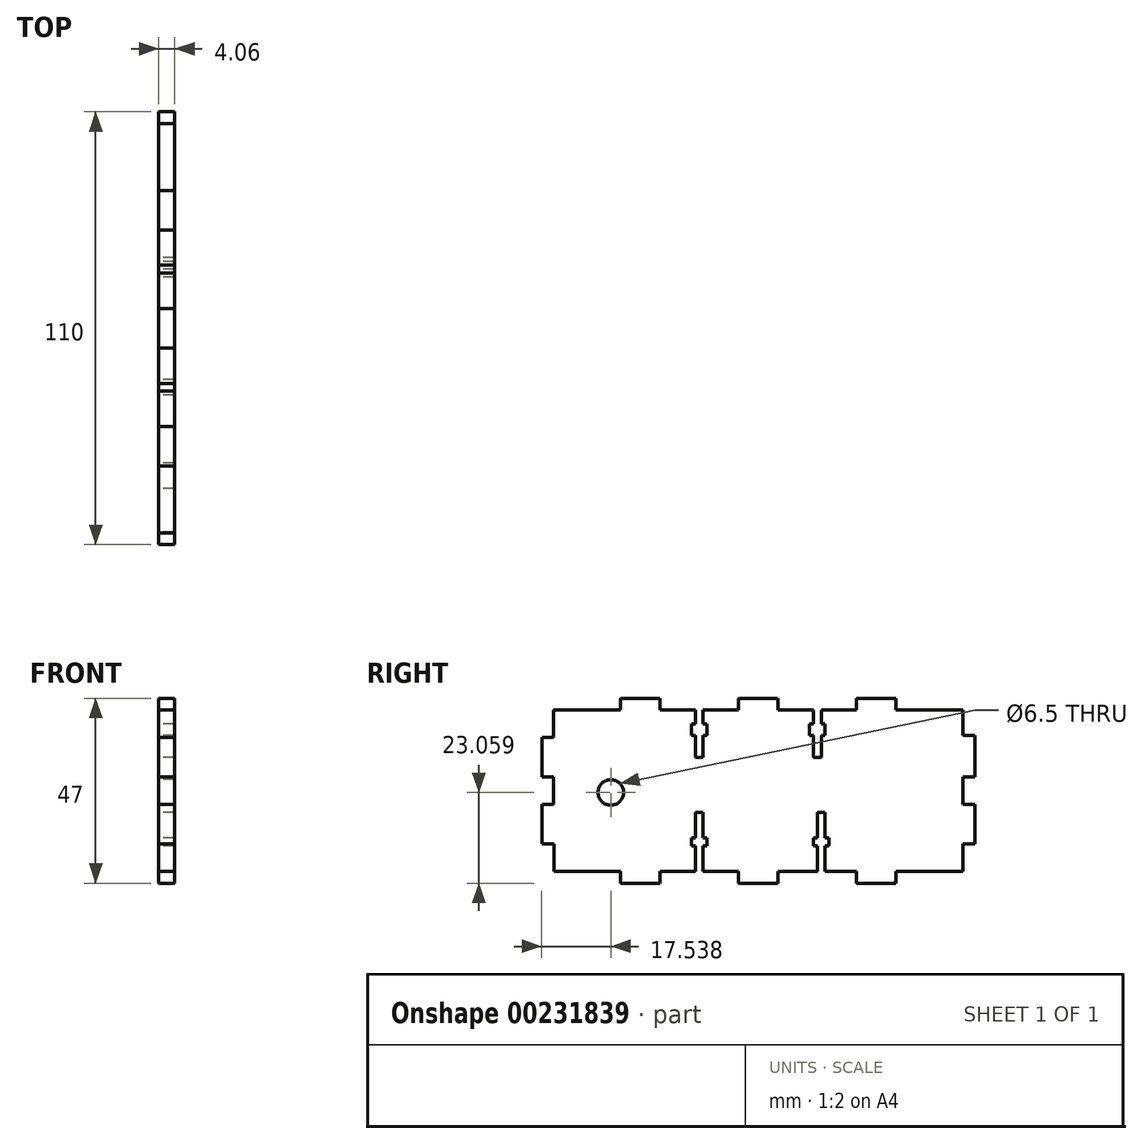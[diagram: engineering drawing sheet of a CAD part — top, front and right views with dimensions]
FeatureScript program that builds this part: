
annotation { "Feature Type Name" : "Feature", "Feature Type Description" : "" }
export const myFeature = defineFeature(function(context is Context, id is Id, definition is map)
    precondition{}
    {
        {
            var Q0;
            Q0=qCreatedBy(makeId("Right.planeOp"),FACE);
            var sketch = newSketch(context, id + "F0", { "sketchPlane" : qUnion([Q0])});
            skLineSegment(sketch, "E0", {"start": v(-50.12, 17.03) * mm, "end": v(-50.12, 7.03) * mm});
            skLineSegment(sketch, "E1", {"start": v(-50.12, 7.03) * mm, "end": v(-47.12, 7.03) * mm});
            skLineSegment(sketch, "E2", {"start": v(-47.12, 7.03) * mm, "end": v(-47.12, 0.03) * mm});
            skLineSegment(sketch, "E3", {"start": v(-47.12, 0.03) * mm, "end": v(-50.12, 0) * mm});
            skLineSegment(sketch, "E4", {"start": v(-50.12, 0) * mm, "end": v(-50.02, -10) * mm});
            skLineSegment(sketch, "E5", {"start": v(-50.02, -10) * mm, "end": v(-47.02, -9.97) * mm});
            skLineSegment(sketch, "E6", {"start": v(-50.12, 17.03) * mm, "end": v(-47.12, 17.03) * mm});
            skLineSegment(sketch, "E7", {"start": v(-47.12, 17.03) * mm, "end": v(-47.12, 24.03) * mm});
            skLineSegment(sketch, "E8", {"start": v(-47.02, -9.97) * mm, "end": v(-46.95, -16.97) * mm});
            skLineSegment(sketch, "E9", {"start": v(-47.12, 24.03) * mm, "end": v(-30.12, 24.03) * mm});
            skLineSegment(sketch, "E10", {"start": v(-30.12, 24.03) * mm, "end": v(-30.12, 27.03) * mm});
            skLineSegment(sketch, "E11", {"start": v(-30.12, 27.03) * mm, "end": v(-20.12, 27.03) * mm});
            skLineSegment(sketch, "E12", {"start": v(-20.12, 27.03) * mm, "end": v(-20.12, 24.03) * mm});
            skLineSegment(sketch, "E13", {"start": v(-20.12, 24.03) * mm, "end": v(-11.12, 24.03) * mm});
            skLineSegment(sketch, "E14", {"start": v(-11.12, 24.03) * mm, "end": v(-11.12, 20.53) * mm});
            skLineSegment(sketch, "E15", {"start": v(-11.12, 20.53) * mm, "end": v(-12.12, 20.53) * mm});
            skLineSegment(sketch, "E16", {"start": v(-12.12, 20.53) * mm, "end": v(-12.12, 17.53) * mm});
            skLineSegment(sketch, "E17", {"start": v(-12.12, 17.53) * mm, "end": v(-11.12, 17.53) * mm});
            skLineSegment(sketch, "E18", {"start": v(-11.12, 17.53) * mm, "end": v(-11.12, 12.03) * mm});
            skLineSegment(sketch, "E19", {"start": v(-11.12, 12.03) * mm, "end": v(-9.12, 12.03) * mm});
            skLineSegment(sketch, "E20", {"start": v(-9.12, 12.03) * mm, "end": v(-9.12, 17.53) * mm});
            skLineSegment(sketch, "E21", {"start": v(-9.12, 17.53) * mm, "end": v(-8.12, 17.53) * mm});
            skLineSegment(sketch, "E22", {"start": v(-8.12, 17.53) * mm, "end": v(-8.12, 20.53) * mm});
            skLineSegment(sketch, "E23", {"start": v(-8.12, 20.53) * mm, "end": v(-9.12, 20.53) * mm});
            skLineSegment(sketch, "E24", {"start": v(-9.12, 20.53) * mm, "end": v(-9.12, 24.03) * mm});
            skLineSegment(sketch, "E25", {"start": v(-9.12, 24.03) * mm, "end": v(-0.12, 24.03) * mm});
            skLineSegment(sketch, "E26", {"start": v(-0.12, 24.03) * mm, "end": v(-0.12, 27.03) * mm});
            skLineSegment(sketch, "E27", {"start": v(-0.12, 27.03) * mm, "end": v(9.88, 27.03) * mm});
            skLineSegment(sketch, "E28", {"start": v(9.88, 27.03) * mm, "end": v(9.88, 24.03) * mm});
            skLineSegment(sketch, "E29", {"start": v(9.88, 24.03) * mm, "end": v(18.88, 24.03) * mm});
            skLineSegment(sketch, "E30", {"start": v(18.88, 24.03) * mm, "end": v(18.88, 20.53) * mm});
            skLineSegment(sketch, "E31", {"start": v(18.88, 20.53) * mm, "end": v(17.88, 20.53) * mm});
            skLineSegment(sketch, "E32", {"start": v(17.88, 20.53) * mm, "end": v(17.88, 17.53) * mm});
            skLineSegment(sketch, "E33", {"start": v(17.88, 17.53) * mm, "end": v(18.88, 17.53) * mm});
            skLineSegment(sketch, "E34", {"start": v(18.88, 17.53) * mm, "end": v(18.88, 12.03) * mm});
            skLineSegment(sketch, "E35", {"start": v(18.88, 12.03) * mm, "end": v(20.88, 12.03) * mm});
            skLineSegment(sketch, "E36", {"start": v(20.88, 12.03) * mm, "end": v(20.88, 17.53) * mm});
            skLineSegment(sketch, "E37", {"start": v(20.88, 17.53) * mm, "end": v(21.88, 17.53) * mm});
            skLineSegment(sketch, "E38", {"start": v(21.88, 17.53) * mm, "end": v(21.88, 20.53) * mm});
            skLineSegment(sketch, "E39", {"start": v(21.88, 20.53) * mm, "end": v(20.88, 20.53) * mm});
            skLineSegment(sketch, "E40", {"start": v(20.88, 20.53) * mm, "end": v(20.88, 24.03) * mm});
            skLineSegment(sketch, "E41", {"start": v(20.88, 24.03) * mm, "end": v(29.88, 24.03) * mm});
            skLineSegment(sketch, "E42", {"start": v(29.88, 24.03) * mm, "end": v(29.88, 27.03) * mm});
            skLineSegment(sketch, "E43", {"start": v(29.88, 27.03) * mm, "end": v(39.88, 27.03) * mm});
            skLineSegment(sketch, "E44", {"start": v(39.88, 27.03) * mm, "end": v(39.88, 24.03) * mm});
            skLineSegment(sketch, "E45", {"start": v(39.88, 24.03) * mm, "end": v(56.88, 24.03) * mm});
            skLineSegment(sketch, "E46", {"start": v(56.88, 24.03) * mm, "end": v(56.88, 17.53) * mm});
            skLineSegment(sketch, "E47", {"start": v(56.88, 17.53) * mm, "end": v(59.88, 17.53) * mm});
            skLineSegment(sketch, "E48", {"start": v(59.88, 17.53) * mm, "end": v(59.88, 7.03) * mm});
            skLineSegment(sketch, "E49", {"start": v(59.88, 7.03) * mm, "end": v(56.88, 7.03) * mm});
            skLineSegment(sketch, "E50", {"start": v(56.88, 7.03) * mm, "end": v(56.88, 0) * mm});
            skLineSegment(sketch, "E51", {"start": v(56.88, 0) * mm, "end": v(59.88, 0) * mm});
            skLineSegment(sketch, "E52", {"start": v(59.88, 0) * mm, "end": v(59.88, -10) * mm});
            skLineSegment(sketch, "E53", {"start": v(59.88, -10) * mm, "end": v(56.88, -10) * mm});
            skLineSegment(sketch, "E54", {"start": v(56.88, -10) * mm, "end": v(56.88, -16.97) * mm});
            skLineSegment(sketch, "E55", {"start": v(56.88, -16.97) * mm, "end": v(39.88, -16.97) * mm});
            skLineSegment(sketch, "E56", {"start": v(39.88, -16.97) * mm, "end": v(39.88, -19.97) * mm});
            skLineSegment(sketch, "E57", {"start": v(39.88, -19.97) * mm, "end": v(29.88, -19.97) * mm});
            skLineSegment(sketch, "E58", {"start": v(29.88, -19.97) * mm, "end": v(29.88, -16.97) * mm});
            skLineSegment(sketch, "E59", {"start": v(29.88, -16.97) * mm, "end": v(21.88, -16.97) * mm});
            skLineSegment(sketch, "E60", {"start": v(21.88, -16.97) * mm, "end": v(21.88, -10.47) * mm});
            skLineSegment(sketch, "E61", {"start": v(21.88, -10.47) * mm, "end": v(22.88, -10.47) * mm});
            skLineSegment(sketch, "E62", {"start": v(22.88, -10.47) * mm, "end": v(22.88, -8.47) * mm});
            skLineSegment(sketch, "E63", {"start": v(22.88, -8.47) * mm, "end": v(21.88, -8.47) * mm});
            skLineSegment(sketch, "E64", {"start": v(21.88, -8.47) * mm, "end": v(21.88, -1.97) * mm});
            skLineSegment(sketch, "E65", {"start": v(21.88, -1.97) * mm, "end": v(19.88, -1.97) * mm});
            skLineSegment(sketch, "E66", {"start": v(19.88, -1.97) * mm, "end": v(19.88, -8.47) * mm});
            skLineSegment(sketch, "E67", {"start": v(19.88, -8.47) * mm, "end": v(18.88, -8.47) * mm});
            skLineSegment(sketch, "E68", {"start": v(18.88, -8.47) * mm, "end": v(18.88, -10.47) * mm});
            skLineSegment(sketch, "E69", {"start": v(18.88, -10.47) * mm, "end": v(19.88, -10.47) * mm});
            skLineSegment(sketch, "E70", {"start": v(19.88, -10.47) * mm, "end": v(19.88, -16.97) * mm});
            skLineSegment(sketch, "E71", {"start": v(19.88, -16.97) * mm, "end": v(9.88, -16.97) * mm});
            skLineSegment(sketch, "E72", {"start": v(9.88, -16.97) * mm, "end": v(9.88, -19.97) * mm});
            skLineSegment(sketch, "E73", {"start": v(9.88, -19.97) * mm, "end": v(-0.12, -19.97) * mm});
            skLineSegment(sketch, "E74", {"start": v(-0.12, -19.97) * mm, "end": v(-0.12, -16.97) * mm});
            skLineSegment(sketch, "E75", {"start": v(-0.12, -16.97) * mm, "end": v(-9.12, -16.97) * mm});
            skLineSegment(sketch, "E76", {"start": v(-9.12, -16.97) * mm, "end": v(-9.12, -10.47) * mm});
            skLineSegment(sketch, "E77", {"start": v(-9.12, -10.47) * mm, "end": v(-8.12, -10.47) * mm});
            skLineSegment(sketch, "E78", {"start": v(-8.12, -10.47) * mm, "end": v(-8.12, -8.47) * mm});
            skLineSegment(sketch, "E79", {"start": v(-8.12, -8.47) * mm, "end": v(-9.12, -8.47) * mm});
            skLineSegment(sketch, "E80", {"start": v(-9.12, -8.47) * mm, "end": v(-9.12, -1.97) * mm});
            skLineSegment(sketch, "E81", {"start": v(-9.12, -1.97) * mm, "end": v(-11.12, -1.97) * mm});
            skLineSegment(sketch, "E82", {"start": v(-11.12, -1.97) * mm, "end": v(-11.12, -8.47) * mm});
            skLineSegment(sketch, "E83", {"start": v(-11.12, -8.47) * mm, "end": v(-12.12, -8.47) * mm});
            skLineSegment(sketch, "E84", {"start": v(-12.12, -8.47) * mm, "end": v(-12.12, -10.47) * mm});
            skLineSegment(sketch, "E85", {"start": v(-12.12, -10.47) * mm, "end": v(-11.12, -10.47) * mm});
            skLineSegment(sketch, "E86", {"start": v(-11.12, -10.47) * mm, "end": v(-11.12, -16.97) * mm});
            skLineSegment(sketch, "E87", {"start": v(-11.12, -16.97) * mm, "end": v(-20.12, -16.97) * mm});
            skLineSegment(sketch, "E88", {"start": v(-20.12, -16.97) * mm, "end": v(-20.12, -19.97) * mm});
            skLineSegment(sketch, "E89", {"start": v(-20.12, -19.97) * mm, "end": v(-30.12, -19.97) * mm});
            skLineSegment(sketch, "E90", {"start": v(-30.12, -19.97) * mm, "end": v(-30.12, -16.97) * mm});
            skLineSegment(sketch, "E91", {"start": v(-30.12, -16.97) * mm, "end": v(-46.95, -16.97) * mm});
            skCircle(sketch, "E92", {"center": v(-32.58, 3.09) * mm, "radius": 3.25 * mm});
            skSolve(sketch);
        }
        {
            var Q0;
            Q0 = qSketchRegion(id + "F0", true);
            extrude(context, id + "F1", {"entities" : qUnion([Q0]), "depth" : 4.06 * mm});
        }
    });
